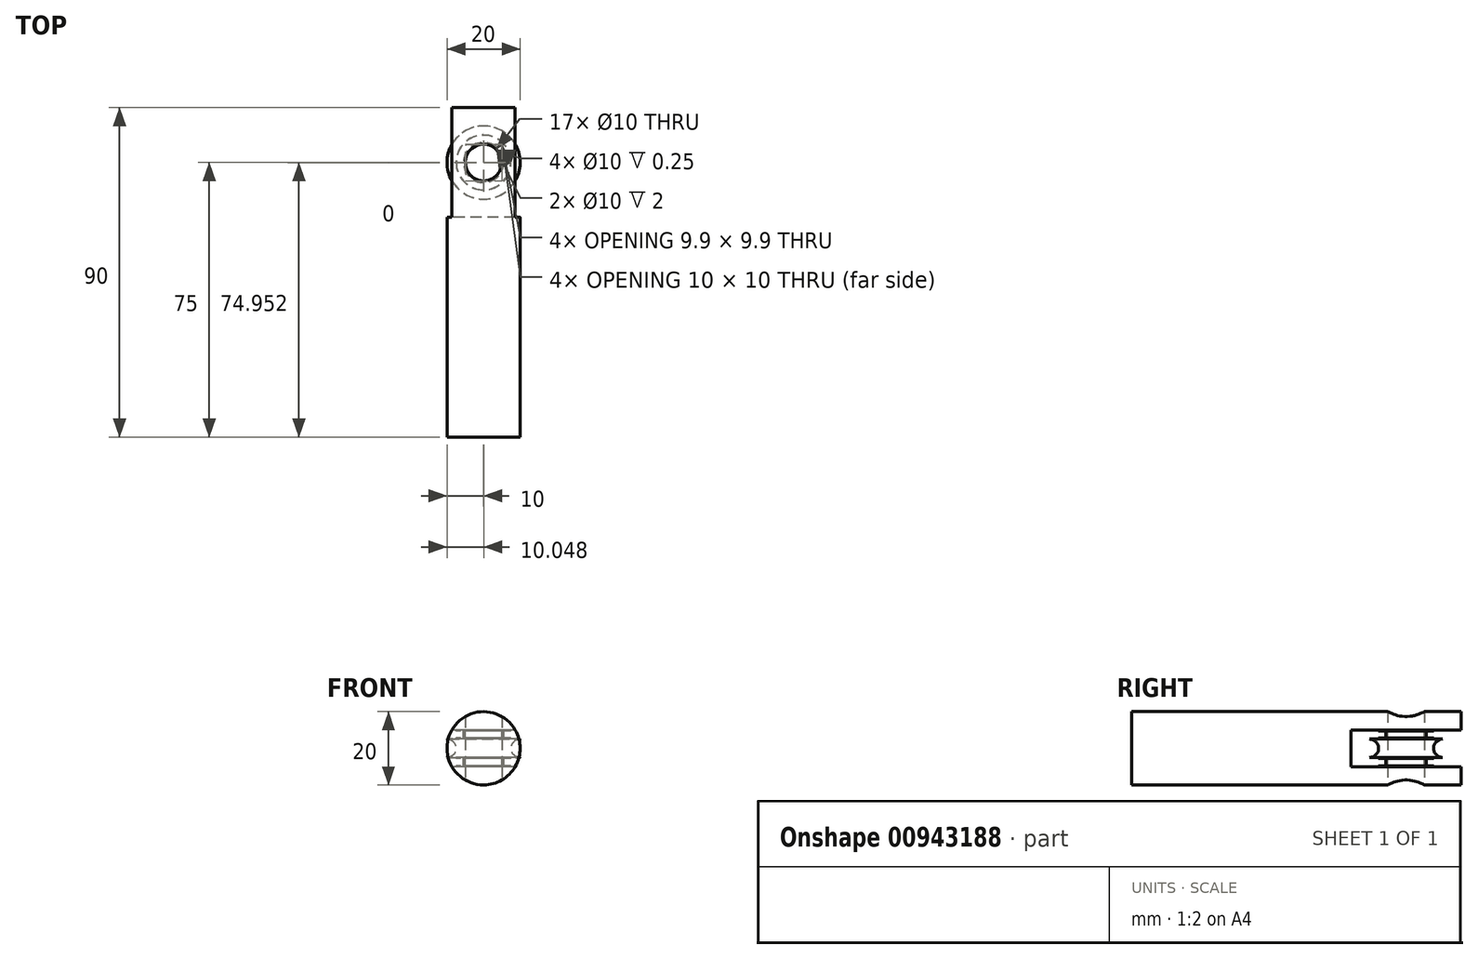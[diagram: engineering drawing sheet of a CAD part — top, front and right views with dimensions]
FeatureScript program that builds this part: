
annotation { "Feature Type Name" : "Feature", "Feature Type Description" : "" }
export const myFeature = defineFeature(function(context is Context, id is Id, definition is map)
    precondition{}
    {
        {
            var Q0;
            Q0=qCreatedBy(makeId("Front.planeOp"),FACE);
            var sketch = newSketch(context, id + "F0", { "sketchPlane" : qUnion([Q0])});
            skCircle(sketch, "E0", {"center": v(0, 0) * mm, "radius": 10 * mm});
            skSolve(sketch);
        }
        {
            var Q0;
            Q0=makeQuery(id+"F0.imprint","IMPRINT",FACE,{"disambiguationData":[TD([[makeQuery(id+"F0.imprint","IMPRINT",EDGE,{"derivedFrom":sQuery(id+"F0.wireOp",EDGE,"E0")}),1.0]])]});
            extrude(context, id + "F1", {"entities" : qUnion([Q0]), "depth" : 75 * mm, "offsetDistance" : 25 * mm, "hasSecondDirection" : true, "secondDirectionOppositeDirection" : true, "secondDirectionDepth" : 15 * mm});
        }
        {
            var Q0;
            Q0=qCreatedBy(makeId("Front.planeOp"),FACE);
            var sketch = newSketch(context, id + "F2", { "sketchPlane" : qUnion([Q0])});
            skLineSegment(sketch, "E1.bottom", {"start": v(15, 5) * mm, "end": v(-15, 5) * mm});
            skLineSegment(sketch, "E1.top", {"start": v(15, -5) * mm, "end": v(-15, -5) * mm});
            skLineSegment(sketch, "E1.left", {"start": v(15, 5) * mm, "end": v(15, -5) * mm});
            skLineSegment(sketch, "E1.right", {"start": v(-15, 5) * mm, "end": v(-15, -5) * mm});
            skPoint(sketch, "E1.middle", {"position": v(0, 0) * mm});
            skSolve(sketch);
        }
        {
            var Q0;
            Q0=makeQuery(id+"F2.imprint","IMPRINT",FACE,{"disambiguationData":[TD([[makeQuery(id+"F2.imprint","IMPRINT",EDGE,{"derivedFrom":sQuery(id+"F2.wireOp",EDGE,"E1.bottom")}),1.0]])]});
            extrude(context, id + "F3", {"entities" : qUnion([Q0]), "operationType" : NewBodyOperationType.REMOVE, "oppositeDirection" : true, "depth" : 15 * mm, "offsetDistance" : 25 * mm, "hasSecondDirection" : true, "secondDirectionOppositeDirection" : false, "secondDirectionDepth" : 15 * mm});
        }
        {
            var Q0;
            Q0=qCreatedBy(makeId("Right.planeOp"),FACE);
            var sketch = newSketch(context, id + "F4", { "sketchPlane" : qUnion([Q0])});
            skLineSegment(sketch, "E2", {"start": v(0, 0) * mm, "end": v(0, 2.5) * mm});
            skLineSegment(sketch, "E3", {"start": v(0, 2.5) * mm, "end": v(10, 2.5) * mm});
            skLineSegment(sketch, "E4", {"start": v(10, 2.5) * mm, "end": v(10, -2.5) * mm});
            skLineSegment(sketch, "E5", {"start": v(10, -2.5) * mm, "end": v(0, -2.5) * mm});
            skLineSegment(sketch, "E6", {"start": v(0, -2.5) * mm, "end": v(0, 0) * mm});
            skArc(sketch, "E7", {"start": v(10, 2.5) * mm, "mid": v(7.5, 0) * mm, "end": v(10, -2.5) * mm});
            skSolve(sketch);
        }
        {
            var Q0;
            Q0=qCreatedBy(makeId("Right.planeOp"),FACE);
            var sketch = newSketch(context, id + "F5", { "sketchPlane" : qUnion([Q0])});
            skLineSegment(sketch, "E8", {"start": v(0, 37.5) * mm, "end": v(0, -27.47) * mm});
            skSolve(sketch);
        }
        {
            var Q0;
            Q0=makeQuery(id+"F4.imprint","IMPRINT",FACE,{"disambiguationData":[TD([[makeQuery(id+"F4.imprint","IMPRINT",EDGE,{"derivedFrom":sQuery(id+"F4.wireOp",EDGE,"E2")}),-1.0]])]});
            var Q1;
            Q1=sQuery(id+"F5.wireOp",EDGE,"E8");
            revolve(context, id + "F6", {"surfaceOperationType" : NewSurfaceOperationType.NEW, "entities" : qUnion([Q0]), "axis" : qUnion([Q1]), "revolveType" : RevolveType.FULL});
        }
        {
            var Q0;
            Q0=qCreatedBy(makeId("Right.planeOp"),FACE);
            var sketch = newSketch(context, id + "F7", { "sketchPlane" : qUnion([Q0])});
            skPoint(sketch, "E9", {"position": v(0, -2.5) * mm});
            skPoint(sketch, "E10", {"position": v(0, -2.75) * mm});
            skLineSegment(sketch, "E11", {"start": v(0, -2.5) * mm, "end": v(0, -2.75) * mm});
            skLineSegment(sketch, "E12", {"start": v(7.5, -2.75) * mm, "end": v(7.5, -2.5) * mm});
            skLineSegment(sketch, "E13", {"start": v(7.5, -2.5) * mm, "end": v(0, -2.5) * mm});
            skLineSegment(sketch, "E14", {"start": v(7.5, -2.75) * mm, "end": v(0, -2.75) * mm});
            skSolve(sketch);
        }
        {
            var Q0;
            Q0=makeQuery(id+"F7.imprint","IMPRINT",FACE,{"disambiguationData":[TD([[makeQuery(id+"F7.imprint","IMPRINT",EDGE,{"derivedFrom":sQuery(id+"F7.wireOp",EDGE,"E11")}),1.0]])]});
            var Q1;
            Q1=sQuery(id+"F5.wireOp",EDGE,"E8");
            revolve(context, id + "F8", {"surfaceOperationType" : NewSurfaceOperationType.NEW, "entities" : qUnion([Q0]), "axis" : qUnion([Q1]), "revolveType" : RevolveType.FULL});
        }
        {
            var Q0;
            Q0=makeQuery(id+"F8.opRevolve","SWEPT_BODY",BODY,{"disambiguationData":[OSD([sQuery(id+"F7.wireOp",EDGE,"E11"),sQuery(id+"F7.wireOp",EDGE,"E12"),sQuery(id+"F7.wireOp",EDGE,"E13"),sQuery(id+"F7.wireOp",EDGE,"E14")])]});
            var Q1;
            Q1=sQuery(id+"F5.wireOp",EDGE,"E8");
            transform(context, id + "F9", {"entities" : qUnion([Q0]), "transformType" : TransformType.TRANSLATION_DISTANCE, "transformDirection" : qUnion([Q1]), "distance" : 5.25 * mm, "oppositeDirection" : true, "makeCopy" : true});
        }
        {
            var Q0;
            Q0=makeQuery(id+"F9.opPattern","COPY",BODY,{"derivedFrom":makeQuery(id+"F8.opRevolve","SWEPT_BODY",BODY,{"disambiguationData":[OSD([sQuery(id+"F7.wireOp",EDGE,"E11"),sQuery(id+"F7.wireOp",EDGE,"E12"),sQuery(id+"F7.wireOp",EDGE,"E13"),sQuery(id+"F7.wireOp",EDGE,"E14")])]}),"instanceName":"1"});
            var Q1;
            Q1=sQuery(id+"F5.wireOp",EDGE,"E8");
            transform(context, id + "F10", {"entities" : qUnion([Q0]), "transformType" : TransformType.TRANSLATION_DISTANCE, "transformDirection" : qUnion([Q1]), "distance" : 7.5 * mm, "makeCopy" : true});
        }
        {
            var Q0;
            Q0=makeQuery(id+"F8.opRevolve","SWEPT_BODY",BODY,{"disambiguationData":[OSD([sQuery(id+"F7.wireOp",EDGE,"E11"),sQuery(id+"F7.wireOp",EDGE,"E12"),sQuery(id+"F7.wireOp",EDGE,"E13"),sQuery(id+"F7.wireOp",EDGE,"E14")])]});
            var Q1;
            Q1=sQuery(id+"F5.wireOp",EDGE,"E8");
            transform(context, id + "F11", {"entities" : qUnion([Q0]), "transformType" : TransformType.TRANSLATION_DISTANCE, "transformDirection" : qUnion([Q1]), "distance" : 7.5 * mm, "oppositeDirection" : true, "makeCopy" : true});
        }
        {
            var Q0;
            Q0=qCreatedBy(makeId("Right.planeOp"),FACE);
            var sketch = newSketch(context, id + "F12", { "sketchPlane" : qUnion([Q0])});
            skPoint(sketch, "E15", {"position": v(0, 2.75) * mm});
            skPoint(sketch, "E16", {"position": v(0, 4.75) * mm});
            skLineSegment(sketch, "E17", {"start": v(0, 2.75) * mm, "end": v(5.5, 2.75) * mm});
            skLineSegment(sketch, "E18", {"start": v(5.5, 2.75) * mm, "end": v(5.5, 4.75) * mm});
            skLineSegment(sketch, "E19", {"start": v(5.5, 4.75) * mm, "end": v(0, 4.75) * mm});
            skLineSegment(sketch, "E20", {"start": v(0, 4.75) * mm, "end": v(0, 2.75) * mm});
            skPoint(sketch, "E21", {"position": v(5, 2.75) * mm});
            skPoint(sketch, "E22", {"position": v(5, 4.75) * mm});
            skLineSegment(sketch, "E23", {"start": v(5, 4.75) * mm, "end": v(5, 2.75) * mm});
            skSolve(sketch);
        }
        {
            var Q0;
            {var subQ0=sQuery(id+"F12.wireOp",EDGE,"E18");Q0=makeQuery(id+"F12.imprint","IMPRINT",FACE,{"disambiguationData":[TD([[makeQuery(id+"F12.imprint","IMPRINT",EDGE,{"derivedFrom":subQ0}),1.0]])]});}
            var Q1;
            Q1=sQuery(id+"F5.wireOp",EDGE,"E8");
            revolve(context, id + "F13", {"surfaceOperationType" : NewSurfaceOperationType.NEW, "entities" : qUnion([Q0]), "axis" : qUnion([Q1]), "revolveType" : RevolveType.FULL});
        }
        {
            var Q0;
            Q0=makeQuery(id+"F13.opRevolve","SWEPT_BODY",BODY,{"disambiguationData":[OSD([sQuery(id+"F12.wireOp",EDGE,"E17"),sQuery(id+"F12.wireOp",EDGE,"E18"),sQuery(id+"F12.wireOp",EDGE,"E19"),sQuery(id+"F12.wireOp",EDGE,"E23")])]});
            var Q1;
            Q1=sQuery(id+"F5.wireOp",EDGE,"E8");
            var Q2;
            Q2=sQuery(id+"F5.wireOp",EDGE,"E8");
            transform(context, id + "F14", {"entities" : qUnion([Q0]), "transformType" : TransformType.TRANSLATION_DISTANCE, "transformDirection" : qUnion([Q2]), "distance" : 7.5 * mm, "makeCopy" : true});
        }
        {
            var Q0;
            Q0=qCreatedBy(makeId("Top.planeOp"),FACE);
            var sketch = newSketch(context, id + "F15", { "sketchPlane" : qUnion([Q0])});
            skCircle(sketch, "E24", {"center": v(0, 0) * mm, "radius": 5 * mm});
            skSolve(sketch);
        }
        {
            var Q0;
            Q0=qSketchRegion(id+"F15",true);
            extrude(context, id + "F16", {"entities" : qUnion([Q0]), "operationType" : NewBodyOperationType.REMOVE, "depth" : 35 * mm, "offsetDistance" : 25 * mm, "symmetric" : true});
        }
    });
